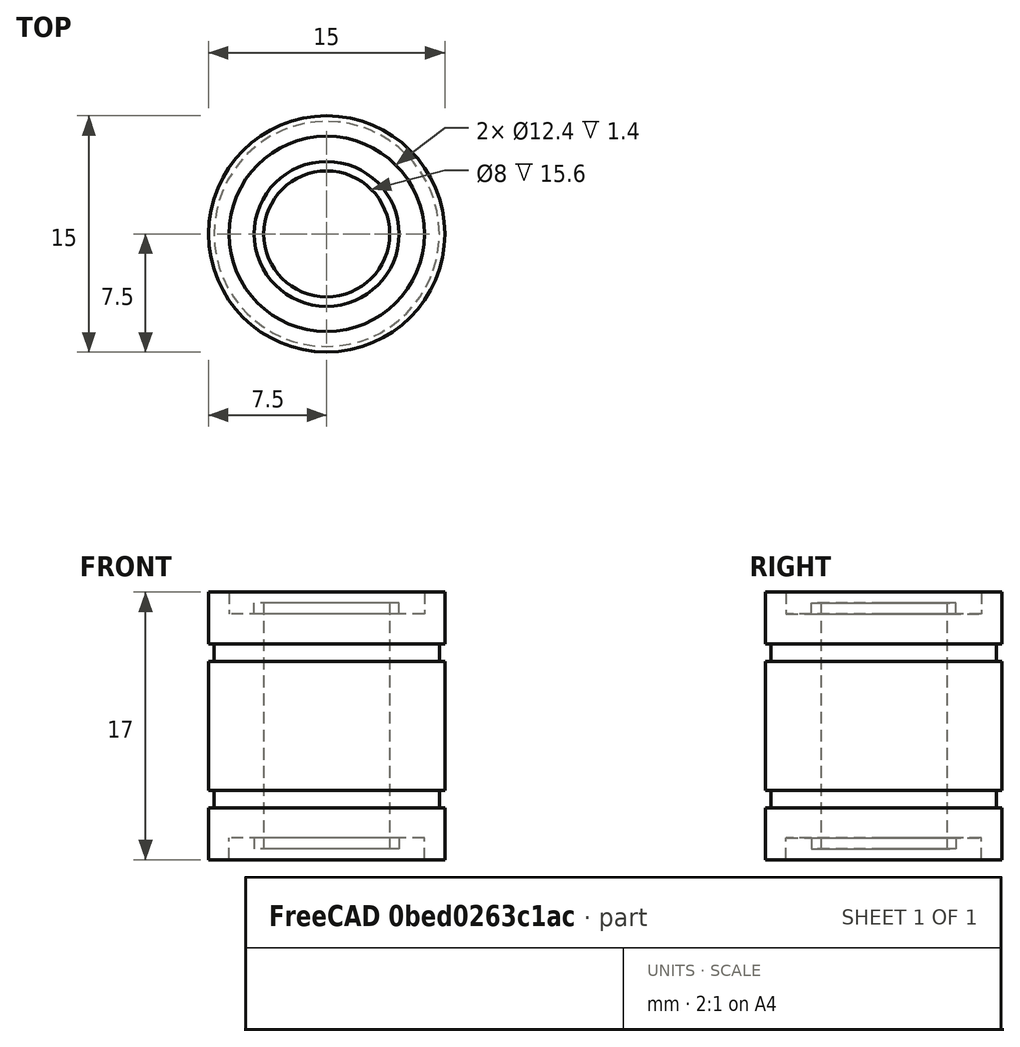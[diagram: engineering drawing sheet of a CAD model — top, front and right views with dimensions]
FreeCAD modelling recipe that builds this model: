
FCSTD DOCUMENT  (FreeCAD 0.16R6703 (Git))
Label: LM8suu
License: CC-BY 3.0
LicenseURL: http://creativecommons.org/licenses/by/3.0/
objects: Sketcher::SketchObject×1, PartDesign::Revolution×1, Part::Feature×1
note: 4 computed .brp shape members not serialized (recipe doc carries the construction recipe); baked Part::Feature solids carry a one-line shape summary decoded from their .brp

FEATURE [Sketcher::SketchObject] Sketch  label="lm8uu-cross-section"
  Placement = pos=(0,0,0) rot=(1,0,0;1.5708rad)
  sketch-geometry (20):
    g0: LineSegment StartX=7.5 StartY=-8.5 StartZ=0 EndX=7.5 EndY=-5.2 EndZ=0
    g1: LineSegment StartX=7.5 StartY=4.1 StartZ=0 EndX=7.15 EndY=4.1 EndZ=0
    g2: LineSegment StartX=7.15 StartY=4.1 StartZ=0 EndX=7.15 EndY=5.2 EndZ=0
    g3: LineSegment StartX=7.15 StartY=5.2 StartZ=0 EndX=7.5 EndY=5.2 EndZ=0
    g4: LineSegment StartX=7.5 StartY=5.2 StartZ=0 EndX=7.5 EndY=8.5 EndZ=0
    g5: LineSegment StartX=7.5 StartY=8.5 StartZ=0 EndX=6.2 EndY=8.5 EndZ=0
    g6: LineSegment StartX=6.2 StartY=8.5 StartZ=0 EndX=6.2 EndY=7.1 EndZ=0
    g7: LineSegment StartX=6.2 StartY=7.1 StartZ=0 EndX=4.6 EndY=7.1 EndZ=0
    g8: LineSegment StartX=4.6 StartY=7.1 StartZ=0 EndX=4.6 EndY=7.8 EndZ=0
    g9: LineSegment StartX=4.6 StartY=7.8 StartZ=0 EndX=4 EndY=7.8 EndZ=0
    g10: LineSegment StartX=4 StartY=7.8 StartZ=0 EndX=4 EndY=-7.8 EndZ=0
    g11: LineSegment StartX=7.5 StartY=-4.1 StartZ=0 EndX=7.15 EndY=-4.1 EndZ=0
    g12: LineSegment StartX=7.15 StartY=-5.2 StartZ=0 EndX=7.5 EndY=-5.2 EndZ=0
    g13: LineSegment StartX=7.5 StartY=-4.1 StartZ=0 EndX=7.5 EndY=4.1 EndZ=0
    g14: LineSegment StartX=7.15 StartY=-4.1 StartZ=0 EndX=7.15 EndY=-5.2 EndZ=0
    g15: LineSegment StartX=7.5 StartY=-8.5 StartZ=0 EndX=6.2 EndY=-8.5 EndZ=0
    g16: LineSegment StartX=6.2 StartY=-8.5 StartZ=0 EndX=6.2 EndY=-7.1 EndZ=0
    g17: LineSegment StartX=6.2 StartY=-7.1 StartZ=0 EndX=4.6 EndY=-7.1 EndZ=0
    g18: LineSegment StartX=4.6 StartY=-7.1 StartZ=0 EndX=4.6 EndY=-7.8 EndZ=0
    g19: LineSegment StartX=4.6 StartY=-7.8 StartZ=0 EndX=4 EndY=-7.8 EndZ=0
  constraints (58):
    c: Coincident(g13,g1)
    c: Coincident(g1,g2)
    c: Vertical(g2)
    c: Coincident(g2,g3)
    c: Coincident(g3,g4)
    c: Vertical(g4)
    c: Coincident(g4,g5)
    c: Coincident(g5,g6)
    c: Vertical(g6)
    c: Coincident(g6,g7)
    c: Horizontal(g7)
    c: Coincident(g7,g8)
    c: Vertical(g8)
    c: Coincident(g8,g9)
    c: Horizontal(g9)
    c: Coincident(g9,g10)
    c: Vertical(g10)
    c: Horizontal(g1)
    c: Horizontal(g5)
    c: Horizontal(g3)
    c: PointOnObject(g3,g0)
    c: Symmetric(g0,g4,g-1)
    c: DistanceY(g4,g0) = -17
    c: DistanceY(g2) = 1.1
    c: DistanceX(g3) = 0.35
    c: DistanceX(g-1,g4) = 7.5
    c: DistanceX(g-1,g9) = 4
    c: DistanceX(g5) = -1.3
    c: DistanceX(g9) = -0.6
    c: DistanceY(g6) = -1.4
    c: DistanceY(g8) = 0.7
    c: Horizontal(g11)
    c: Horizontal(g12)
    c: Coincident(g13,g11)
    c: Tangent(g0,g13)
    c: Coincident(g12,g0)
    c: PointOnObject(g14,g11)
    c: Coincident(g14,g12)
    c: Vertical(g14)
    c: Symmetric(g1,g11,g-1)
    c: DistanceY(g13) = 8.2
    c: Equal(g14,g2)
    c: Coincident(g0,g15)
    c: Horizontal(g15)
    c: Coincident(g15,g16)
    c: Vertical(g16)
    c: Coincident(g16,g17)
    c: Horizontal(g17)
    c: Coincident(g17,g18)
    c: Vertical(g18)
    c: Coincident(g18,g19)
    c: Horizontal(g19)
    c: Coincident(g10,g19)
    c: Symmetric(g10,g9,g-1)
    c: Symmetric(g16,g6,g-1)
    c: Symmetric(g17,g7,g-1)
    c: Coincident(g14,g11)
    c: PointOnObject(g11,g2)
FEATURE [PartDesign::Revolution] Revolution  label="LM8uu"
  Angle = 360
  Axis = (0,0,1)
  Base = (0,0,0)
  Placement = pos=(0,0,0) rot=(1,0,0;1.5708rad)
  ReferenceAxis = -> Sketch [V_Axis]
  Reversed = true
  Sketch = -> Sketch
FEATURE [Part::Feature] Revolution001  label="LM8uu001"
  Placement = pos=(0,0,0) rot=(1,0,0;1.5708rad)
  shape: bbox 15 x 15 x 17 mm, 20 faces (baked)
